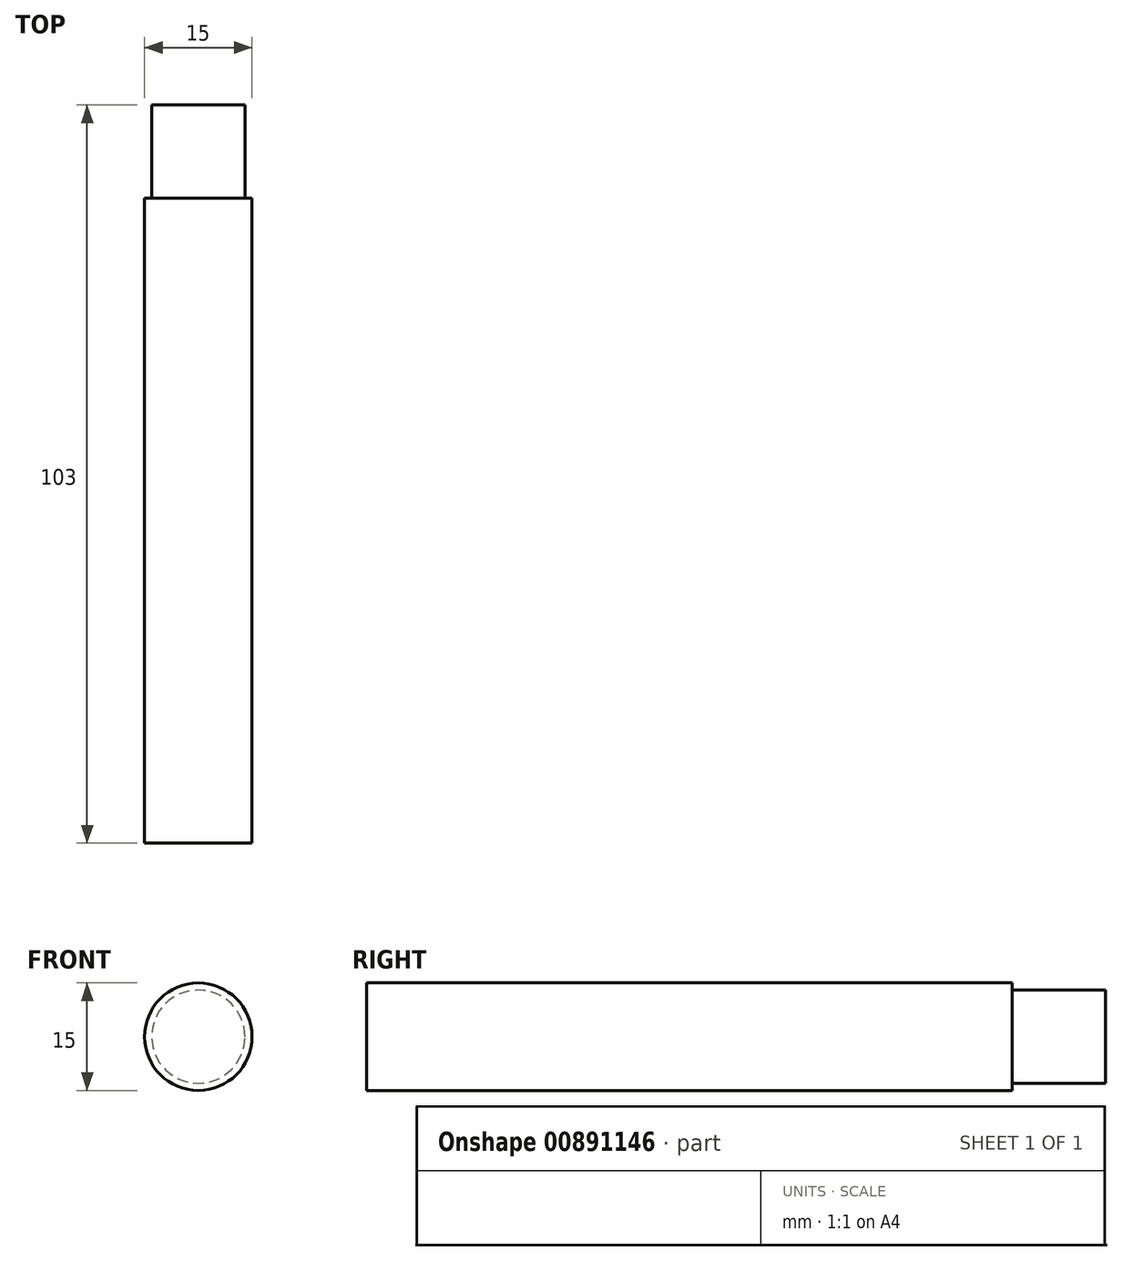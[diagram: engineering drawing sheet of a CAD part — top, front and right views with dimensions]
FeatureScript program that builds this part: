
annotation { "Feature Type Name" : "Feature", "Feature Type Description" : "" }
export const myFeature = defineFeature(function(context is Context, id is Id, definition is map)
    precondition{}
    {
        {
            var Q0;
            Q0=qCreatedBy(makeId("Front.planeOp"),FACE);
            var sketch = newSketch(context, id + "F0", { "sketchPlane" : qUnion([Q0])});
            skCircle(sketch, "E0", {"center": v(0, 0) * mm, "radius": 7.5 * mm});
            skSolve(sketch);
        }
        {
            var Q0;
            Q0 = qSketchRegion(id + "F0", true);
            extrude(context, id + "F1", {"entities" : qUnion([Q0]), "endBound" : BoundingType.SYMMETRIC, "depth" : 90 * mm, "offsetDistance" : 25 * mm});
        }
        {
            var Q0;
            Q0=makeQuery(id+"F1.opExtrude","CAP_FACE",FACE,{"disambiguationData":[OSD([sQuery(id+"F0.wireOp",EDGE,"E0")])],"isStart":true});
            var sketch = newSketch(context, id + "F2", { "sketchPlane" : qUnion([Q0])});
            skCircle(sketch, "E1", {"center": v(0, 0) * mm, "radius": 6.5 * mm});
            skSolve(sketch);
        }
        {
            var Q0;
            Q0 = qSketchRegion(id + "F2", true);
            extrude(context, id + "F3", {"entities" : qUnion([Q0]), "operationType" : NewBodyOperationType.ADD, "depth" : 13 * mm, "offsetDistance" : 25 * mm});
        }
    });
